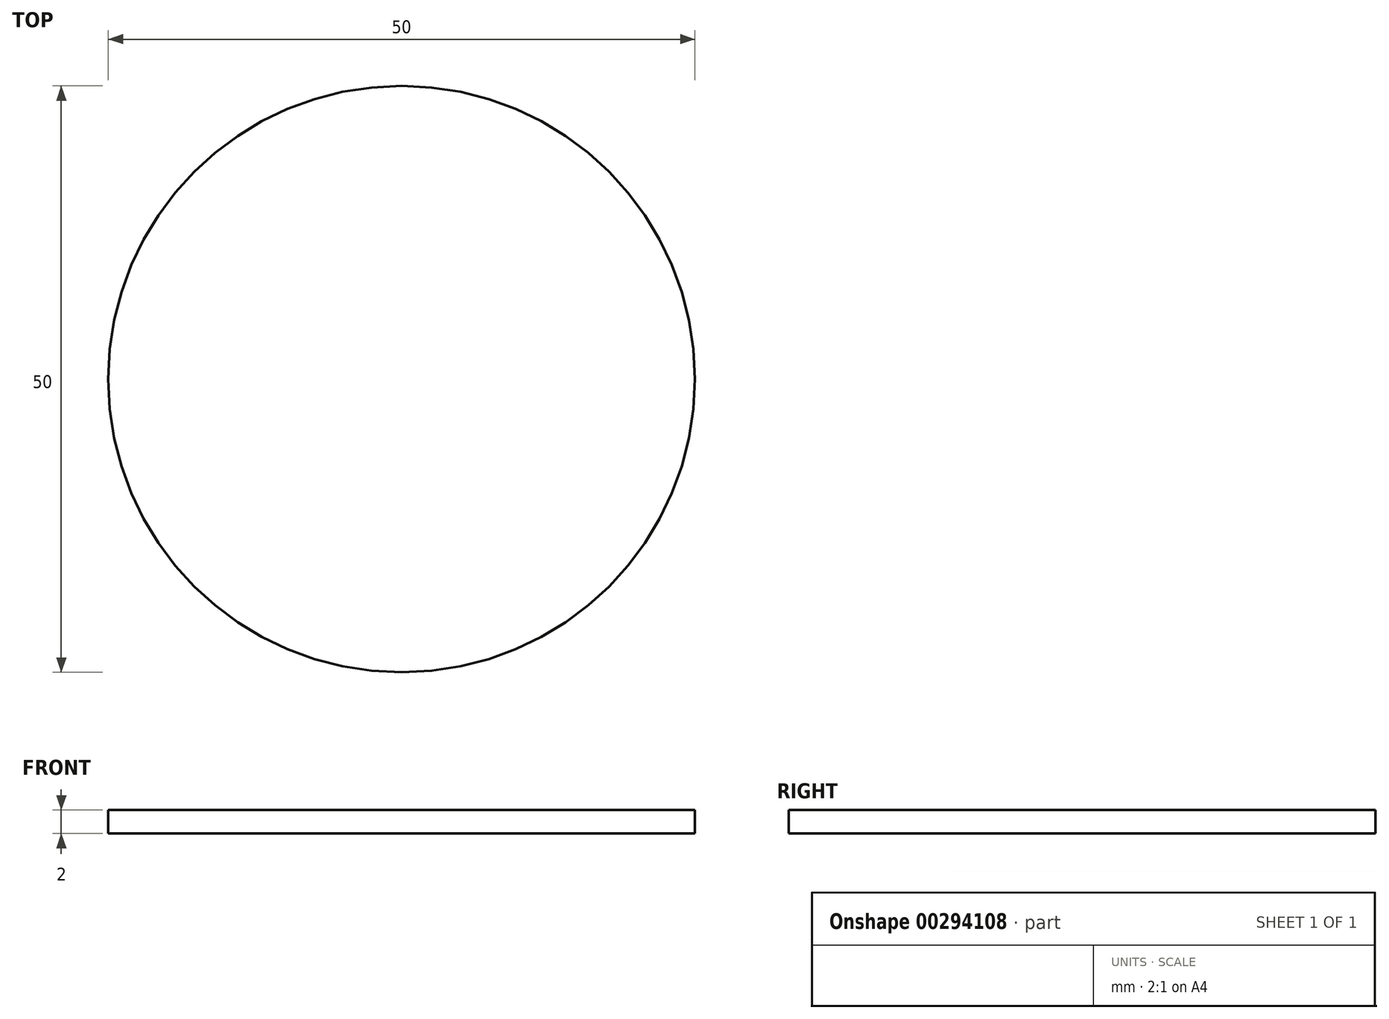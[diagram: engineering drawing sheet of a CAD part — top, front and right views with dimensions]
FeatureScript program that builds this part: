
annotation { "Feature Type Name" : "Feature", "Feature Type Description" : "" }
export const myFeature = defineFeature(function(context is Context, id is Id, definition is map)
    precondition{}
    {
        {
            var Q0;
            Q0=qCreatedBy(makeId("Top.planeOp"),FACE);
            var sketch = newSketch(context, id + "F0", { "sketchPlane" : qUnion([Q0])});
            skCircle(sketch, "E0", {"center": v(0, 0) * mm, "radius": 25 * mm});
            skSolve(sketch);
        }
        {
            var Q0;
            Q0 = qSketchRegion(id + "F0", true);
            extrude(context, id + "F1", {"entities" : qUnion([Q0]), "depth" : 2 * mm});
        }
    });
